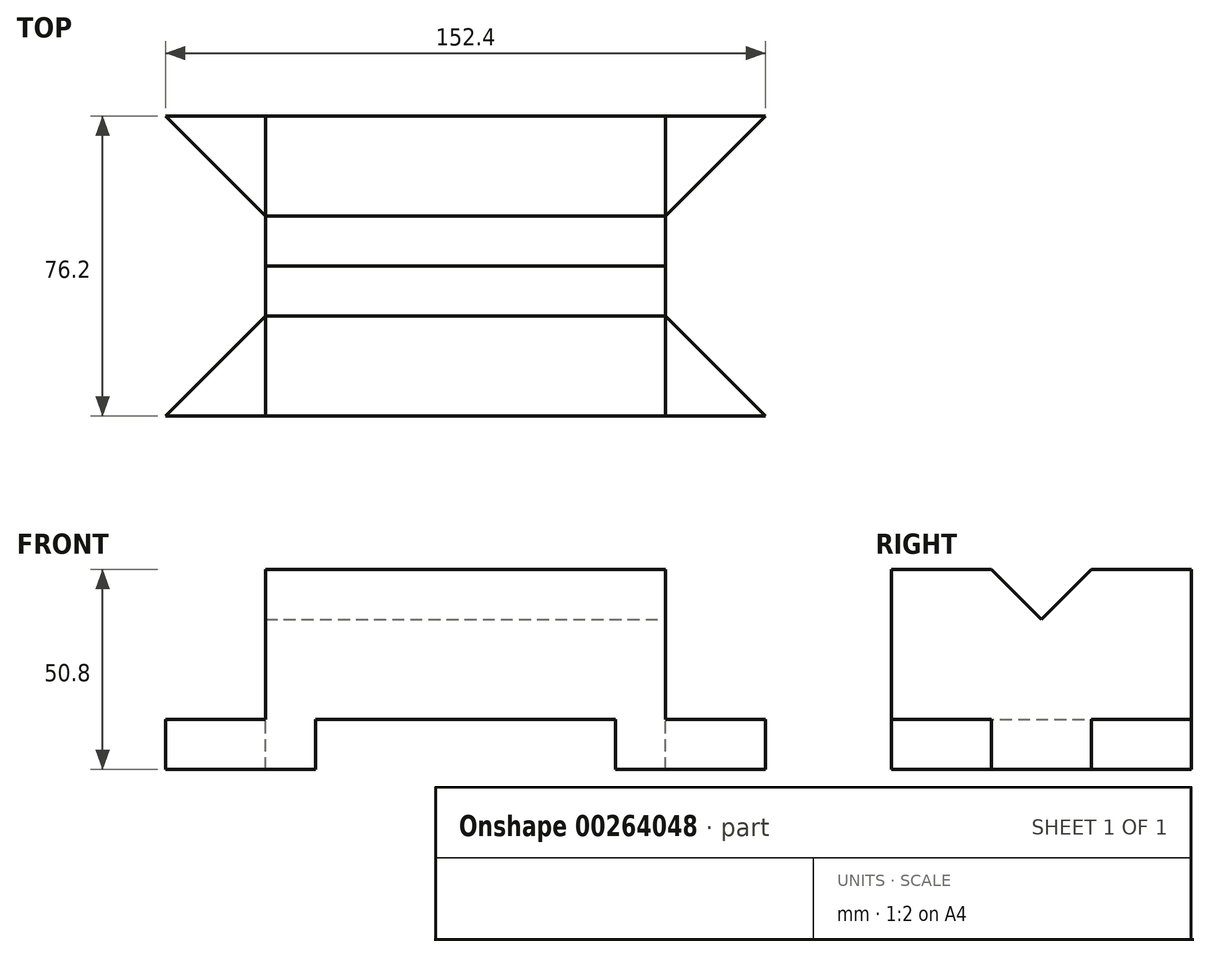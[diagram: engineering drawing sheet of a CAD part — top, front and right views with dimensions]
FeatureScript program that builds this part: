
annotation { "Feature Type Name" : "Feature", "Feature Type Description" : "" }
export const myFeature = defineFeature(function(context is Context, id is Id, definition is map)
    precondition{}
    {
        {
            var Q0;
            Q0=qCreatedBy(makeId("Front.planeOp"),FACE);
            var sketch = newSketch(context, id + "F0", { "sketchPlane" : qUnion([Q0])});
            skLineSegment(sketch, "E0.bottom", {"start": v(-75.98, 0) * mm, "end": v(-37.88, 0) * mm});
            skLineSegment(sketch, "E0.top", {"start": v(-75.98, 12.7) * mm, "end": v(-37.88, 12.7) * mm});
            skLineSegment(sketch, "E0.left", {"start": v(-75.98, 0) * mm, "end": v(-75.98, 12.7) * mm});
            skLineSegment(sketch, "E0.right", {"start": v(-37.88, 0) * mm, "end": v(-37.88, 12.7) * mm});
            skLineSegment(sketch, "E1", {"start": v(-37.88, 12.7) * mm, "end": v(-50.58, 12.7) * mm});
            skLineSegment(sketch, "E2", {"start": v(-50.58, 12.7) * mm, "end": v(-50.58, 50.8) * mm});
            skLineSegment(sketch, "E3", {"start": v(-37.88, 12.7) * mm, "end": v(38.32, 12.7) * mm});
            skLineSegment(sketch, "E4", {"start": v(38.32, 12.7) * mm, "end": v(38.32, 0) * mm});
            skLineSegment(sketch, "E5", {"start": v(38.32, 0) * mm, "end": v(76.42, 0) * mm});
            skLineSegment(sketch, "E6", {"start": v(76.42, 0) * mm, "end": v(76.42, 12.7) * mm});
            skLineSegment(sketch, "E7", {"start": v(38.32, 12.7) * mm, "end": v(51.02, 12.7) * mm});
            skLineSegment(sketch, "E8", {"start": v(51.02, 12.7) * mm, "end": v(51.02, 50.8) * mm});
            skLineSegment(sketch, "E9", {"start": v(76.42, 12.7) * mm, "end": v(51.02, 12.7) * mm});
            skLineSegment(sketch, "E10", {"start": v(-50.58, 50.8) * mm, "end": v(51.02, 50.8) * mm});
            skSolve(sketch);
        }
        {
            var Q0;
            Q0 = qSketchRegion(id + "F0", true);
            extrude(context, id + "F1", {"entities" : qUnion([Q0]), "depth" : 76.2 * mm});
        }
        {
            var Q0;
            Q0=makeQuery(id+"F1.opExtrude","SWEPT_FACE",FACE,{"disambiguationData":[OSD([sQuery(id+"F0.wireOp",EDGE,"E8")])]});
            var sketch = newSketch(context, id + "F2", { "sketchPlane" : qUnion([Q0])});
            skLineSegment(sketch, "E11", {"start": v(-76.2, 50.8) * mm, "end": v(-50.8, 50.8) * mm});
            skLineSegment(sketch, "E12", {"start": v(0, 50.8) * mm, "end": v(-25.4, 50.8) * mm});
            skLineSegment(sketch, "E13", {"start": v(-25.4, 50.8) * mm, "end": v(-38.1, 50.8) * mm});
            skLineSegment(sketch, "E14", {"start": v(-38.1, 50.8) * mm, "end": v(-38.1, 38.1) * mm});
            skLineSegment(sketch, "E15", {"start": v(-25.4, 50.8) * mm, "end": v(-38.1, 38.1) * mm});
            skLineSegment(sketch, "E16", {"start": v(-50.8, 50.8) * mm, "end": v(-38.1, 38.1) * mm});
            skSolve(sketch);
        }
        {
            var Q0;
            {var subQ0=sQuery(id+"F2.wireOp",EDGE,"E14");Q0=makeQuery(id+"F2.imprint","IMPRINT",FACE,{"disambiguationData":[TD([[makeQuery(id+"F2.imprint","IMPRINT",EDGE,{"derivedFrom":subQ0}),-1.0]])]});}
            var Q1;
            Q1=makeQuery(id+"F2.imprint","IMPRINT",FACE,{"disambiguationData":[TD([[makeQuery(id+"F2.imprint","IMPRINT",EDGE,{"derivedFrom":sQuery(id+"F2.wireOp",EDGE,"E13")}),-1.0]])]});
            extrude(context, id + "F3", {"entities" : qUnion([Q0, Q1]), "operationType" : NewBodyOperationType.REMOVE, "oppositeDirection" : true, "depth" : 101.6 * mm});
        }
        {
            var Q0;
            Q0=makeQuery(id+"F1.opExtrude","SWEPT_FACE",FACE,{"disambiguationData":[OSD([sQuery(id+"F0.wireOp",EDGE,"E9")])]});
            var sketch = newSketch(context, id + "F4", { "sketchPlane" : qUnion([Q0])});
            skLineSegment(sketch, "E17", {"start": v(51.02, -76.2) * mm, "end": v(51.02, -50.8) * mm});
            skLineSegment(sketch, "E18", {"start": v(51.02, 0) * mm, "end": v(51.02, -25.4) * mm});
            skLineSegment(sketch, "E19", {"start": v(51.02, -50.8) * mm, "end": v(76.42, -76.2) * mm});
            skLineSegment(sketch, "E20", {"start": v(51.02, -25.4) * mm, "end": v(76.42, 0) * mm});
            skSolve(sketch);
        }
        {
            var Q0;
            {var subQ0=sQuery(id+"F4.wireOp",EDGE,"E19");Q0=makeQuery(id+"F4.imprint","IMPRINT",FACE,{"disambiguationData":[TD([[makeQuery(id+"F4.imprint","IMPRINT",EDGE,{"derivedFrom":subQ0}),1.0]])]});}
            extrude(context, id + "F5", {"entities" : qUnion([Q0]), "operationType" : NewBodyOperationType.REMOVE, "oppositeDirection" : true, "depth" : 25.4 * mm});
        }
        {
            var Q0;
            Q0=makeQuery(id+"F1.opExtrude","SWEPT_FACE",FACE,{"disambiguationData":[OSD([sQuery(id+"F0.wireOp",EDGE,"E0.top")])]});
            var sketch = newSketch(context, id + "F6", { "sketchPlane" : qUnion([Q0])});
            skLineSegment(sketch, "E21", {"start": v(-50.58, 0) * mm, "end": v(-50.58, -25.4) * mm});
            skLineSegment(sketch, "E22", {"start": v(-50.58, -76.2) * mm, "end": v(-50.58, -50.8) * mm});
            skLineSegment(sketch, "E23", {"start": v(-50.58, -25.4) * mm, "end": v(-75.98, 0) * mm});
            skLineSegment(sketch, "E24", {"start": v(-50.58, -50.8) * mm, "end": v(-75.98, -76.2) * mm});
            skSolve(sketch);
        }
        {
            var Q0;
            {var subQ0=sQuery(id+"F6.wireOp",EDGE,"E23");Q0=makeQuery(id+"F6.imprint","IMPRINT",FACE,{"disambiguationData":[TD([[makeQuery(id+"F6.imprint","IMPRINT",EDGE,{"derivedFrom":subQ0}),1.0]])]});}
            extrude(context, id + "F7", {"entities" : qUnion([Q0]), "operationType" : NewBodyOperationType.REMOVE, "oppositeDirection" : true, "depth" : 25.4 * mm});
        }
    });
